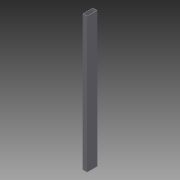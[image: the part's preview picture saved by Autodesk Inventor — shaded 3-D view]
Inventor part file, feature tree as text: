
AUTODESK INVENTOR PART (.ipt)
format: ipt  version: 2014 (Build 180170000, 170)  size: 80,384 bytes
history: native  units: in
note: dims shown in document units (in); Inventor stores cm internally (conversion verified against a paired STEP export)
features: other x2, extrude x1, sketch x1
ambient origin geometry x8: Origin, YZ Plane, XZ Plane, XY Plane, X Axis, Y Axis, Z Axis, Center Point
bodies: Solid1 (feature_tree)
feature tree (4):
  other  "Table"
  other  "squareTube1.5x2-01"
  extrude  "Extrusion1"  Depth=4.0in
  sketch  "Sketch1"  dims[d0=1.75in d1=4.0in d2=0.125in d4=0.0in]
